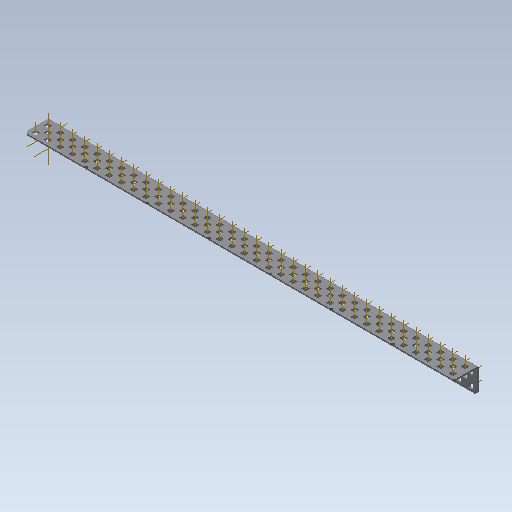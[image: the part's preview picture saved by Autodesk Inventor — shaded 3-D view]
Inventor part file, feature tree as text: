
AUTODESK INVENTOR PART (.ipt)
format: ipt  version: 2020 (Build 240168000, 168)  size: 2,355,712 bytes
history: native  units: in
note: dims shown in document units (in); Inventor stores cm internally (conversion verified against a paired STEP export)
features: other x215, pattern_linear x4, sheet_metal_op x1, extrude x1, imported_body x1, sketch x1
ambient origin geometry x8: Origin, YZ Plane, XZ Plane, XY Plane, X Axis, Y Axis, Z Axis, Center Point
bodies: Body1 (feature_tree)
feature tree (223):
  sheet_metal_op  "Fold1"
  other  "L-Channel"
  extrude  "length cut"  Depth=0.5in
  other  "top out axis"
  other  "top inner axis"
  other  "back out axis"
  other  "back inner axis"
  pattern_linear  "top outer axes"  Count1=2 Spacing1=0.5in
  pattern_linear  "top inner axes"  Spacing1=0.5in  [1 undecoded]
  pattern_linear  "back outer axes"  Count1=2 Spacing1=0.5in
  pattern_linear  "back inner axes"  Spacing1=0.5in  [1 undecoded]
  other  "right plane"
  imported_body  "Base1"
  sketch  "Sketch1"  dims[d1=0.0in d4=0.5in d5=0.7874in d7=0.5in d10=0.5in d13=0.5in d14=0.7874in d16=0.5in d19=0.5in d20=-17.5in d21=0.0in d22=0.0in d23=0.0in d24=0.0in d25=0.0in d26=0.0in]
  other  "Work Point1"
  other  "Work Point2"
  other  "Work Point3"
  other  "Work Point4"
  other  "Work Axis5"
  other  "Work Axis6"
  other  "Work Axis7"
  other  "Work Axis8"
  other  "Work Axis11"
  other  "Work Axis12"
  other  "Work Axis13"
  other  "Work Axis14"
  other  "Work Axis15"
  other  "Work Axis18"
  other  "Work Axis19"
  other  "Work Axis20"
  other  "Work Axis23"
  other  "Work Axis24"
  other  "Work Axis25"
  other  "Work Axis26"
  other  "Work Axis29"
  other  "Work Axis30"
  other  "Work Axis31"
  other  "Work Axis32"
  other  "Work Axis33"
  other  "Work Axis36"
  other  "Work Axis37"
  other  "Work Axis38"
  other  "Work Axis41"
  other  "Work Axis42"
  other  "Work Axis43"
  other  "Work Axis44"
  other  "Work Axis45"
  other  "Work Axis46"
  other  "Work Axis47"
  other  "Work Axis48"
  other  "Work Axis49"
  other  "Work Axis50"
  other  "Work Axis51"
  other  "Work Axis52"
  other  "Work Axis53"
  other  "Work Axis54"
  other  "Work Axis55"
  other  "Work Axis56"
  other  "Work Axis57"
  other  "Work Axis58"
  other  "Work Axis59"
  other  "Work Axis60"
  other  "Work Axis61"
  other  "Work Axis62"
  other  "Work Axis63"
  other  "Work Axis64"
  other  "Work Axis65"
  other  "Work Axis66"
  other  "Work Axis67"
  other  "Work Axis68"
  other  "Work Axis69"
  other  "Work Axis70"
  other  "Work Axis71"
  other  "Work Axis72"
  other  "Work Axis73"
  other  "Work Axis74"
  other  "Work Axis75"
  other  "Work Axis76"
  other  "Work Axis77"
  other  "Work Axis78"
  other  "Work Axis79"
  other  "Work Axis80"
  other  "Work Axis81"
  other  "Work Axis82"
  other  "Work Axis83"
  other  "Work Axis84"
  other  "Work Axis85"
  other  "Work Axis86"
  other  "Work Axis87"
  other  "Work Axis88"
  other  "Work Axis89"
  other  "Work Axis90"
  other  "Work Axis91"
  other  "Work Axis92"
  other  "Work Axis93"
  other  "Work Axis94"
  other  "Work Axis95"
  other  "Work Axis96"
  other  "Work Axis97"
  other  "Work Axis98"
  other  "Work Axis99"
  other  "Work Axis100"
  other  "Work Axis101"
  other  "Work Axis102"
  other  "Work Axis103"
  other  "Work Axis104"
  other  "Work Axis105"
  other  "Work Axis106"
  other  "Work Axis107"
  other  "Work Axis108"
  other  "Work Axis109"
  other  "Work Axis110"
  other  "Work Axis111"
  other  "Work Axis112"
  other  "Work Axis113"
  other  "Work Axis114"
  other  "Work Axis115"
  other  "Work Axis116"
  other  "Work Axis117"
  other  "Work Axis118"
  other  "Work Axis119"
  other  "Work Axis120"
  other  "Work Axis121"
  other  "Work Axis122"
  other  "Work Axis123"
  other  "Work Axis124"
  other  "Work Axis125"
  other  "Work Axis126"
  other  "Work Axis127"
  other  "Work Axis128"
  other  "Work Axis129"
  other  "Work Axis130"
  other  "Work Axis131"
  other  "Work Axis132"
  other  "Work Axis133"
  other  "Work Axis134"
  other  "Work Axis135"
  other  "Work Axis136"
  other  "Work Axis137"
  other  "Work Axis138"
  other  "Work Axis139"
  other  "Work Axis140"
  other  "Work Axis141"
  other  "Work Axis142"
  other  "Work Axis143"
  other  "Work Axis144"
  other  "Work Axis145"
  other  "Work Axis146"
  other  "Work Axis147"
  other  "Work Axis148"
  other  "Work Axis149"
  other  "Work Axis150"
  other  "Work Axis151"
  other  "Work Axis152"
  other  "Work Axis153"
  other  "Work Axis154"
  other  "Work Axis155"
  other  "Work Axis156"
  other  "Work Axis157"
  other  "Work Axis158"
  other  "Work Axis159"
  other  "Work Axis160"
  other  "left plane"
  other  "Work Axis161"
  other  "Work Axis162"
  other  "Work Axis163"
  other  "Work Axis164"
  other  "Work Axis165"
  other  "Work Axis166"
  other  "Work Axis167"
  other  "Work Axis168"
  other  "Work Axis169"
  other  "Work Axis170"
  other  "Work Axis171"
  other  "Work Axis172"
  other  "Work Axis173"
  other  "Work Axis174"
  other  "Work Axis175"
  other  "Work Axis176"
  other  "Work Axis177"
  other  "Work Axis178"
  other  "Work Axis179"
  other  "Work Axis180"
  other  "Work Axis181"
  other  "Work Axis182"
  other  "Work Axis183"
  other  "Work Axis184"
  other  "Work Axis185"
  other  "Work Axis186"
  other  "Work Axis187"
  other  "Work Axis188"
  other  "Work Axis189"
  other  "Work Axis190"
  other  "Work Axis191"
  other  "Work Axis192"
  other  "Work Axis193"
  other  "Work Axis194"
  other  "Work Axis195"
  other  "Work Axis196"
  other  "Work Axis197"
  other  "Work Axis198"
  other  "Work Axis199"
  other  "Work Axis200"
  other  "Work Axis201"
  other  "Work Axis202"
  other  "Work Axis203"
  other  "Work Axis204"
  other  "Work Axis205"
  other  "Work Axis206"
  other  "Work Axis207"
  other  "Work Axis208"
  other  "Work Axis209"
  other  "Work Axis210"
  other  "Work Axis211"
  other  "Work Axis212"
  other  "Work Axis213"
  other  "Work Axis214"
  other  "Work Axis215"
  other  "Work Axis216"
  other  "Work Axis217"
  other  "Work Axis218"
  other  "Work Axis219"
  other  "Work Axis220"
note: 2 required parameter values undecoded (feature->parameter linkage not recoverable at this tier; creation-order binding heuristic only, values carry confidence <= 0.55)
